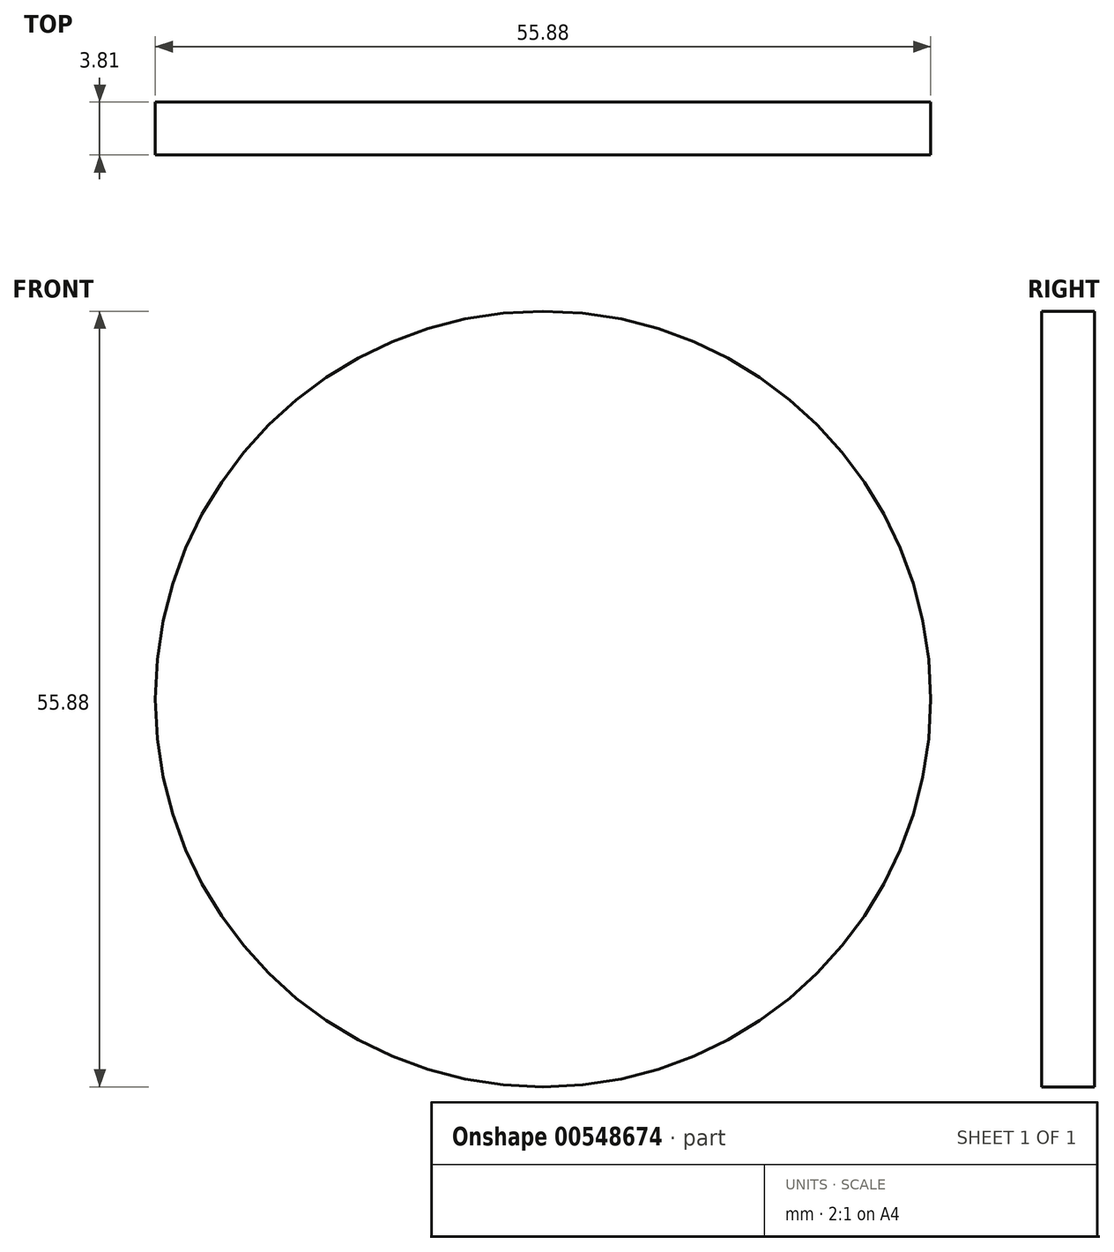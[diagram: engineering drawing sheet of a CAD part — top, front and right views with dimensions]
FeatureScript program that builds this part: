
annotation { "Feature Type Name" : "Feature", "Feature Type Description" : "" }
export const myFeature = defineFeature(function(context is Context, id is Id, definition is map)
    precondition{}
    {
        {
            var Q0;
            Q0=qCreatedBy(makeId("Front.planeOp"),FACE);
            var sketch = newSketch(context, id + "F0", { "sketchPlane" : qUnion([Q0])});
            skCircle(sketch, "E0", {"center": v(0, 0) * mm, "radius": 27.94 * mm});
            skSolve(sketch);
        }
        {
            var Q0;
            Q0=makeQuery(id+"F0.imprint","IMPRINT",FACE,{"disambiguationData":[TD([[makeQuery(id+"F0.imprint","IMPRINT",EDGE,{"derivedFrom":sQuery(id+"F0.wireOp",EDGE,"E0")}),1.0]])]});
            extrude(context, id + "F1", {"entities" : qUnion([Q0]), "depth" : 3.8 * mm, "offsetDistance" : 25.4 * mm});
        }
    });
